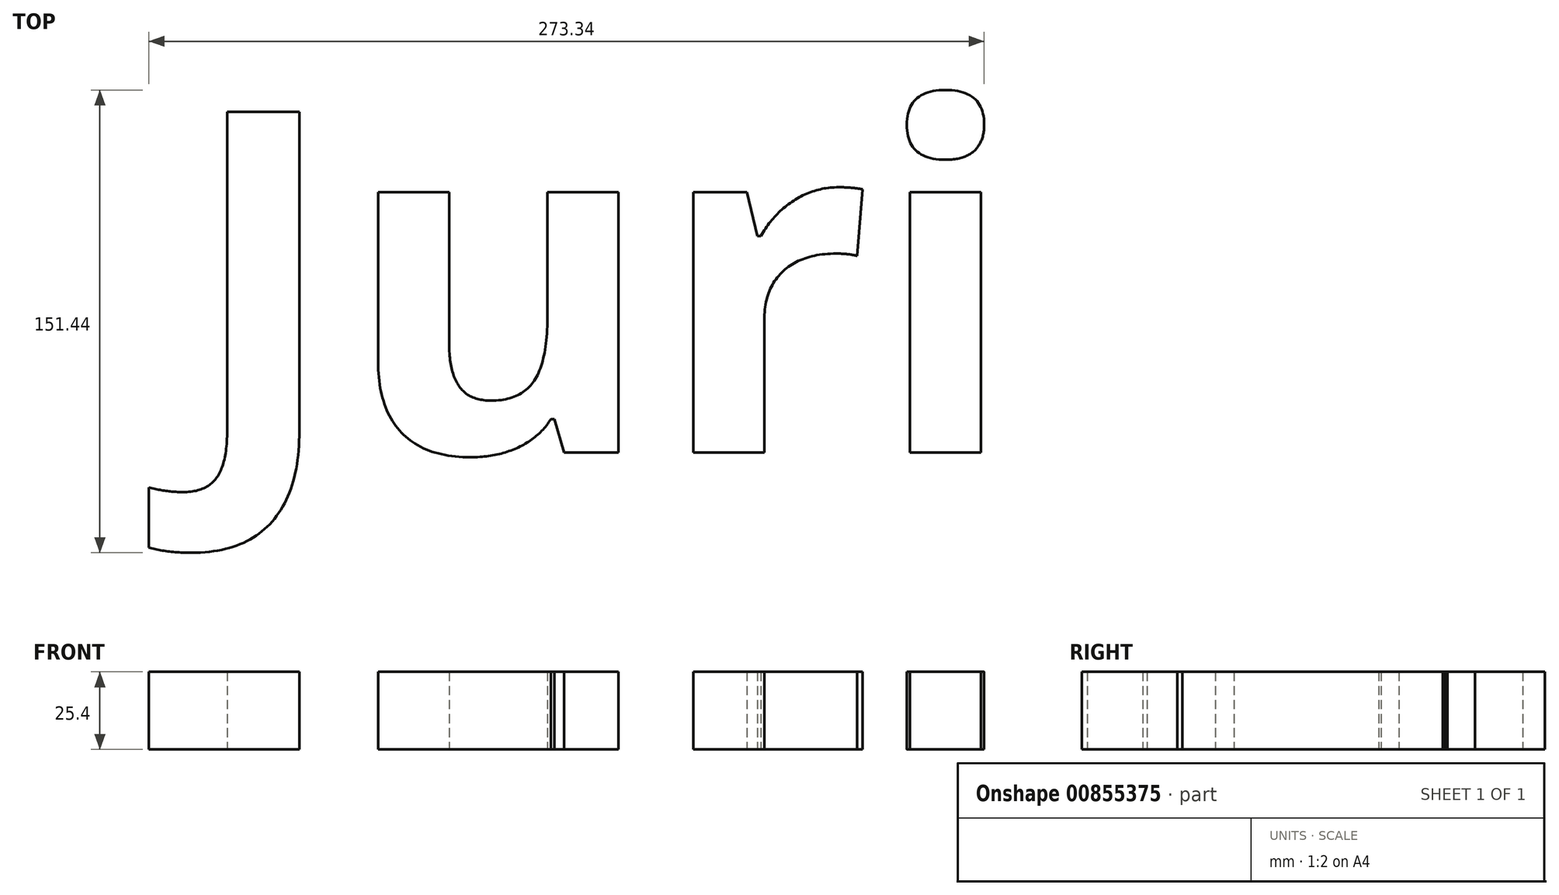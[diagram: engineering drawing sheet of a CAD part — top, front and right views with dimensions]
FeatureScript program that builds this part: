
annotation { "Feature Type Name" : "Feature", "Feature Type Description" : "" }
export const myFeature = defineFeature(function(context is Context, id is Id, definition is map)
    precondition{}
    {
        {
            var Q0;
            Q0=qCreatedBy(makeId("Top.planeOp"),FACE);
            var sketch = newSketch(context, id + "F0", { "sketchPlane" : qUnion([Q0])});
            skText(sketch, "E0", { "text": "Juri", "fontName": "OpenSans-Bold.ttf"});
            const initialGuessF0  = {"E0": [-0.083, -0.05422, 1, 0, 0.11243]};
            skSetInitialGuess(sketch, initialGuessF0);
            skSolve(sketch);
        }
        {
            var Q0;
            Q0 = qSketchRegion(id + "F0", true);
            extrude(context, id + "F1", {"entities" : qUnion([Q0]), "depth" : 25.4 * mm, "offsetDistance" : 25.4 * mm});
        }
    });
